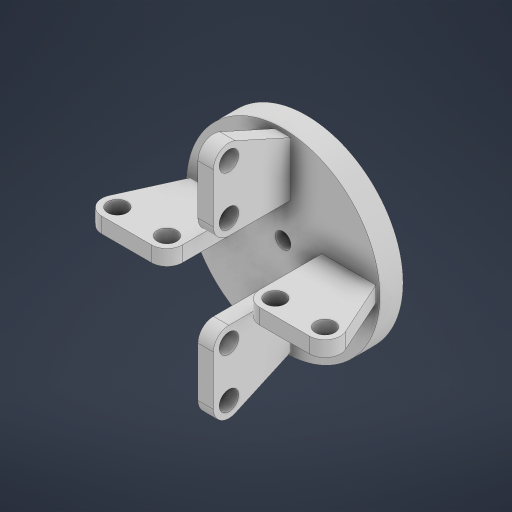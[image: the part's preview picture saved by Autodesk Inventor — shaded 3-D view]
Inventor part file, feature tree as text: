
AUTODESK INVENTOR PART (.ipt)
format: ipt  version: 2023 (Build 270158000, 158)  size: 302,080 bytes
history: native  units: mm
features: extrude x5, sketch x5, pattern_circular x2, fillet x1, direct_edit x1, other x1
ambient origin geometry x8: Origin, YZ Plane, XZ Plane, XY Plane, X Axis, Y Axis, Z Axis, Center Point
bodies: Solid1 (feature_tree)
feature tree (15):
  extrude  "Extrusion1"  Depth=25.0mm TaperAngle=0.0deg
  extrude  "Extrusion2"  Depth=2.0mm TaperAngle=0.0deg
  extrude  "Extrusion3"  Depth=2.0mm TaperAngle=360.0deg
  extrude  "Extrusion5"  Depth=10.0mm
  pattern_circular  "Circular Pattern3"  [2 undecoded]
  fillet  "Fillet2"  Radius=40.0mm
  extrude  "Extrusion6"  Depth=2.5mm
  pattern_circular  "Circular Pattern4"  [2 undecoded]
  direct_edit  "Direct Edit1"
  sketch  "Sketch1"  dims[d0=25.0mm d1=3.0mm d2=0.0mm]
  sketch  "Sketch2"  dims[d3=2.0mm d4=3.0mm d5=0.0mm]
  sketch  "Sketch3"  dims[d8=2.0mm d9=40.0mm d11=360.0deg]
  sketch  "Sketch5"  dims[d13=10.0mm d14=0.0mm d26=7.0mm]
  sketch  "Sketch6"  dims[d27=10.0mm d28=0.0mm d29=2.0mm d30=40.0mm d31=360.0deg d33=2.5mm d34=2.5mm d35=10.0mm d36=0.0mm d37=40.0mm d38=360.0deg d40=20.0mm d41=10.0mm d42=10.0mm]
  other  "Scale1"
note: 4 required parameter values undecoded (feature->parameter linkage not recoverable at this tier; creation-order binding heuristic only, values carry confidence <= 0.55)
